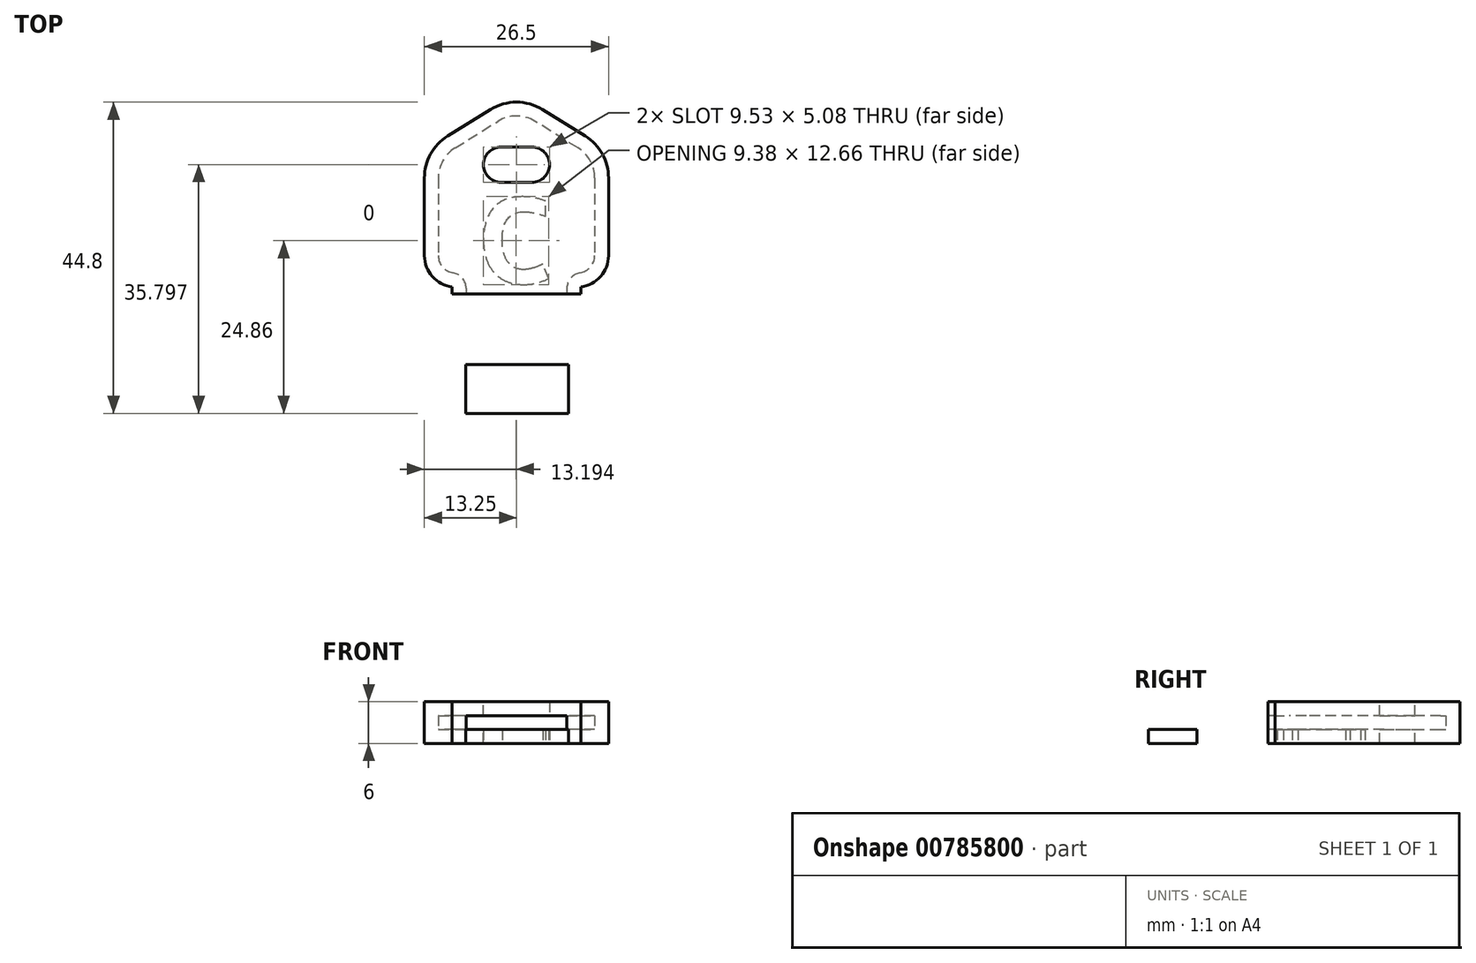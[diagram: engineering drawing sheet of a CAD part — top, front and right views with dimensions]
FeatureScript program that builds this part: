
annotation { "Feature Type Name" : "Feature", "Feature Type Description" : "" }
export const myFeature = defineFeature(function(context is Context, id is Id, definition is map)
    precondition{}
    {
        {
            var Q0;
            Q0=qCreatedBy(makeId("Top.planeOp"),FACE);
            var sketch = newSketch(context, id + "F0", { "sketchPlane" : qUnion([Q0])});
            skLineSegment(sketch, "E0.bottom", {"start": v(-11.25, 18.93) * mm, "end": v(11.25, 18.93) * mm});
            skLineSegment(sketch, "E0.top", {"start": v(-11.25, -7.57) * mm, "end": v(11.25, -7.57) * mm});
            skLineSegment(sketch, "E0.left", {"start": v(-11.25, 18.93) * mm, "end": v(-11.25, -7.57) * mm});
            skLineSegment(sketch, "E0.right", {"start": v(11.25, 18.93) * mm, "end": v(11.25, -7.57) * mm});
            skSolve(sketch);
        }
        {
            var Q0;
            Q0 = qSketchRegion(id + "F0", true);
            extrude(context, id + "F1", {"entities" : qUnion([Q0]), "depth" : 2 * mm, "offsetDistance" : 25.4 * mm});
        }
        {
            var Q0;
            Q0=makeQuery(id+"F1.opExtrude","SWEPT_EDGE",EDGE,{"disambiguationData":[OSD([sQuery(id+"F0.wireOp",EDGE,"E0.bottom"),sQuery(id+"F0.wireOp",EDGE,"E0.left")])]});
            var Q1;
            Q1=makeQuery(id+"F1.opExtrude","SWEPT_EDGE",EDGE,{"disambiguationData":[OSD([sQuery(id+"F0.wireOp",EDGE,"E0.bottom"),sQuery(id+"F0.wireOp",EDGE,"E0.right")])]});
            chamfer(context, id + "F2", {"entities" : qUnion([Q0, Q1]), "chamferType" : ChamferType.TWO_OFFSETS, "width1" : 22.5 * mm / 2, "oppositeDirection" : true, "width2" : 7 * mm, "tangentPropagation" : true});
        }
        {
            var Q0;
            {var subQ0=sQuery(id+"F0.wireOp",EDGE,"E0.bottom");Q0=makeQuery(id+"F2.opChamfer","BLEND_EDGE",EDGE,{"blendedFrom":[makeQuery(id+"F1.opExtrude","SWEPT_EDGE",EDGE,{"disambiguationData":[OSD([subQ0,sQuery(id+"F0.wireOp",EDGE,"E0.left")])]}),makeQuery(id+"F1.opExtrude","SWEPT_EDGE",EDGE,{"disambiguationData":[OSD([subQ0,sQuery(id+"F0.wireOp",EDGE,"E0.right")])]})],"blendedInto":[]});}
            var Q1;
            {var subQ0=sQuery(id+"F0.wireOp",EDGE,"E0.left");Q1=makeQuery(id+"F2.opChamfer","BLEND_EDGE",EDGE,{"blendedFrom":[makeQuery(id+"F1.opExtrude","SWEPT_EDGE",EDGE,{"disambiguationData":[OSD([sQuery(id+"F0.wireOp",EDGE,"E0.bottom"),subQ0])]}),makeQuery(id+"F1.opExtrude","SWEPT_FACE",FACE,{"disambiguationData":[OSD([subQ0])]})],"blendedInto":[makeQuery(id+"F1.opExtrude","SWEPT_FACE",FACE,{"disambiguationData":[OSD([subQ0])]})]});}
            var Q2;
            {var subQ0=sQuery(id+"F0.wireOp",EDGE,"E0.right");Q2=makeQuery(id+"F2.opChamfer","BLEND_EDGE",EDGE,{"blendedFrom":[makeQuery(id+"F1.opExtrude","SWEPT_EDGE",EDGE,{"disambiguationData":[OSD([sQuery(id+"F0.wireOp",EDGE,"E0.bottom"),subQ0])]}),makeQuery(id+"F1.opExtrude","SWEPT_FACE",FACE,{"disambiguationData":[OSD([subQ0])]})],"blendedInto":[makeQuery(id+"F1.opExtrude","SWEPT_FACE",FACE,{"disambiguationData":[OSD([subQ0])]})]});}
            fillet(context, id + "F3", {"entities" : qUnion([Q0, Q1, Q2]), "radius" : 5.08 * mm, "tangentPropagation" : true, "allowEdgeOverflow" : false});
        }
        {
            var Q0;
            Q0=makeQuery(id+"F1.opExtrude","CAP_FACE",FACE,{"disambiguationData":[OSD([sQuery(id+"F0.wireOp",EDGE,"E0.bottom"),sQuery(id+"F0.wireOp",EDGE,"E0.top"),sQuery(id+"F0.wireOp",EDGE,"E0.left"),sQuery(id+"F0.wireOp",EDGE,"E0.right")])],"isStart":false});
            var sketch = newSketch(context, id + "F4", { "sketchPlane" : qUnion([Q0])});
            skLineSegment(sketch, "E1.bottom", {"start": v(-15.5, -4.57) * mm, "end": v(-7.25, -4.57) * mm});
            skLineSegment(sketch, "E1.top", {"start": v(-15.5, -14.03) * mm, "end": v(-7.25, -14.03) * mm});
            skLineSegment(sketch, "E1.left", {"start": v(-15.5, -4.57) * mm, "end": v(-15.5, -14.03) * mm});
            skLineSegment(sketch, "E1.right", {"start": v(-7.25, -4.57) * mm, "end": v(-7.25, -14.03) * mm});
            skLineSegment(sketch, "E2.bottom", {"start": v(7.25, -4.57) * mm, "end": v(18.47, -4.57) * mm});
            skLineSegment(sketch, "E2.top", {"start": v(7.25, -15.42) * mm, "end": v(18.47, -15.42) * mm});
            skLineSegment(sketch, "E2.left", {"start": v(7.25, -4.57) * mm, "end": v(7.25, -15.42) * mm});
            skLineSegment(sketch, "E2.right", {"start": v(18.47, -4.57) * mm, "end": v(18.47, -15.42) * mm});
            skSolve(sketch);
        }
        {
            var Q0;
            Q0 = qSketchRegion(id + "F4", true);
            extrude(context, id + "F5", {"entities" : qUnion([Q0]), "operationType" : NewBodyOperationType.REMOVE, "oppositeDirection" : true, "depth" : 25.4 * mm, "offsetDistance" : 25.4 * mm});
        }
        {
            var Q0;
            Q0=makeQuery(id+"F5.boolean.opBoolean","INTERSECT",EDGE,{"derivedFrom":[makeQuery(id+"F1.opExtrude","SWEPT_FACE",FACE,{"disambiguationData":[OSD([sQuery(id+"F0.wireOp",EDGE,"E0.left")])]}),makeQuery(id+"F5.opExtrude","SWEPT_FACE",FACE,{"disambiguationData":[OSD([sQuery(id+"F4.wireOp",EDGE,"E1.bottom")])]})]});
            var Q1;
            Q1=makeQuery(id+"F5.boolean.opBoolean","INTERSECT",EDGE,{"derivedFrom":[makeQuery(id+"F1.opExtrude","SWEPT_FACE",FACE,{"disambiguationData":[OSD([sQuery(id+"F0.wireOp",EDGE,"E0.right")])]}),makeQuery(id+"F5.opExtrude","SWEPT_FACE",FACE,{"disambiguationData":[OSD([sQuery(id+"F4.wireOp",EDGE,"E2.bottom")])]})]});
            fillet(context, id + "F6", {"entities" : qUnion([Q0, Q1]), "radius" : 2.5 * mm, "tangentPropagation" : true, "allowEdgeOverflow" : false});
        }
        {
            var Q0;
            Q0=makeQuery(id+"F5.boolean.opBoolean","COPY",EDGE,{"derivedFrom":makeQuery(id+"F5.opExtrude","SWEPT_EDGE",EDGE,{"disambiguationData":[OSD([sQuery(id+"F4.wireOp",EDGE,"E1.bottom"),sQuery(id+"F4.wireOp",EDGE,"E1.right")])]})});
            var Q1;
            Q1=makeQuery(id+"F5.boolean.opBoolean","COPY",EDGE,{"derivedFrom":makeQuery(id+"F5.opExtrude","SWEPT_EDGE",EDGE,{"disambiguationData":[OSD([sQuery(id+"F4.wireOp",EDGE,"E2.bottom"),sQuery(id+"F4.wireOp",EDGE,"E2.left")])]})});
            fillet(context, id + "F7", {"entities" : qUnion([Q0, Q1]), "radius" : 2.25 * mm, "tangentPropagation" : true, "allowEdgeOverflow" : false});
        }
        {
            var Q0;
            Q0=makeQuery(id+"F1.opExtrude","CAP_FACE",FACE,{"disambiguationData":[OSD([sQuery(id+"F0.wireOp",EDGE,"E0.bottom"),sQuery(id+"F0.wireOp",EDGE,"E0.top"),sQuery(id+"F0.wireOp",EDGE,"E0.left"),sQuery(id+"F0.wireOp",EDGE,"E0.right")])],"isStart":false});
            var sketch = newSketch(context, id + "F8", { "sketchPlane" : qUnion([Q0])});
            skArc(sketch, "E3.0", {"start": v(-9.91, 15.12) * mm, "mid": v(-12.36, 12.55) * mm, "end": v(-13.25, 9.1) * mm});
            skLineSegment(sketch, "E3.1", {"start": v(9.25, -7.57) * mm, "end": v(9.25, -6.54) * mm});
            skLineSegment(sketch, "E3.2", {"start": v(-9.25, -7.57) * mm, "end": v(9.25, -7.57) * mm});
            skLineSegment(sketch, "E3.3", {"start": v(-9.25, -6.54) * mm, "end": v(-9.25, -7.57) * mm});
            skArc(sketch, "E3.4", {"start": v(-13.25, -2.07) * mm, "mid": v(-12.1, -5.07) * mm, "end": v(-9.25, -6.54) * mm});
            skArc(sketch, "E3.5", {"start": v(9.25, -6.54) * mm, "mid": v(12.1, -5.07) * mm, "end": v(13.25, -2.07) * mm});
            skLineSegment(sketch, "E3.6", {"start": v(-13.25, 9.1) * mm, "end": v(-13.25, -2.07) * mm});
            skLineSegment(sketch, "E3.7", {"start": v(13.25, -2.07) * mm, "end": v(13.25, 9.1) * mm});
            skArc(sketch, "E3.8", {"start": v(13.25, 9.1) * mm, "mid": v(12.36, 12.55) * mm, "end": v(9.91, 15.12) * mm});
            skLineSegment(sketch, "E3.9", {"start": v(9.91, 15.12) * mm, "end": v(3.74, 18.96) * mm});
            skArc(sketch, "E3.10", {"start": v(3.74, 18.96) * mm, "mid": v(0, 20.03) * mm, "end": v(-3.74, 18.96) * mm});
            skLineSegment(sketch, "E3.11", {"start": v(-3.74, 18.96) * mm, "end": v(-9.91, 15.12) * mm});
            skSolve(sketch);
        }
        {
            var Q0;
            Q0 = qSketchRegion(id + "F8", true);
            extrude(context, id + "F9", {"entities" : qUnion([Q0]), "depth" : 2 * mm, "offsetDistance" : 25.4 * mm, "hasSecondDirection" : true, "secondDirectionOppositeDirection" : true, "secondDirectionDepth" : 4 * mm});
        }
        {
            var Q0;
            Q0=makeQuery(id+"F1.opExtrude","SWEPT_BODY",BODY,{"disambiguationData":[OSD([sQuery(id+"F0.wireOp",EDGE,"E0.bottom"),sQuery(id+"F0.wireOp",EDGE,"E0.top"),sQuery(id+"F0.wireOp",EDGE,"E0.left"),sQuery(id+"F0.wireOp",EDGE,"E0.right")])]});
            var Q1;
            Q1=makeQuery(id+"F9.opExtrude","SWEPT_BODY",BODY,{"disambiguationData":[OSD([sQuery(id+"F8.wireOp",EDGE,"E3.0"),sQuery(id+"F8.wireOp",EDGE,"E3.1"),sQuery(id+"F8.wireOp",EDGE,"E3.2"),sQuery(id+"F8.wireOp",EDGE,"E3.3"),sQuery(id+"F8.wireOp",EDGE,"E3.4"),sQuery(id+"F8.wireOp",EDGE,"E3.5"),sQuery(id+"F8.wireOp",EDGE,"E3.6"),sQuery(id+"F8.wireOp",EDGE,"E3.7"),sQuery(id+"F8.wireOp",EDGE,"E3.8"),sQuery(id+"F8.wireOp",EDGE,"E3.9"),sQuery(id+"F8.wireOp",EDGE,"E3.10"),sQuery(id+"F8.wireOp",EDGE,"E3.11")])]});
            booleanBodies(context, id + "F10", {"operationType" : BooleanOperationType.SUBTRACTION, "tools" : qUnion([Q0]), "targets" : qUnion([Q1])});
        }
        {
            var Q0;
            Q0=makeQuery(id+"F9.opExtrude","CAP_FACE",FACE,{"disambiguationData":[OSD([sQuery(id+"F8.wireOp",EDGE,"E3.0"),sQuery(id+"F8.wireOp",EDGE,"E3.1"),sQuery(id+"F8.wireOp",EDGE,"E3.2"),sQuery(id+"F8.wireOp",EDGE,"E3.3"),sQuery(id+"F8.wireOp",EDGE,"E3.4"),sQuery(id+"F8.wireOp",EDGE,"E3.5"),sQuery(id+"F8.wireOp",EDGE,"E3.6"),sQuery(id+"F8.wireOp",EDGE,"E3.7"),sQuery(id+"F8.wireOp",EDGE,"E3.8"),sQuery(id+"F8.wireOp",EDGE,"E3.9"),sQuery(id+"F8.wireOp",EDGE,"E3.10"),sQuery(id+"F8.wireOp",EDGE,"E3.11")])],"isStart":true});
            var sketch = newSketch(context, id + "F11", { "sketchPlane" : qUnion([Q0])});
            skText(sketch, "E4", { "text": "C", "fontName": "OpenSans-Bold.ttf"});
            const initialGuessF11  = {"E4": [-0.00575, -0.00625, 1, 0, 0.01242]};
            skSetInitialGuess(sketch, initialGuessF11);
            skSolve(sketch);
        }
        {
            var Q0;
            Q0 = qSketchRegion(id + "F11", true);
            extrude(context, id + "F12", {"entities" : qUnion([Q0]), "operationType" : NewBodyOperationType.REMOVE, "endBound" : BoundingType.UP_TO_NEXT, "oppositeDirection" : true, "depth" : 25.4 * mm, "offsetDistance" : 25.4 * mm});
        }
        {
            var Q0;
            Q0=makeQuery(id+"F9.opExtrude","CAP_FACE",FACE,{"disambiguationData":[OSD([sQuery(id+"F8.wireOp",EDGE,"E3.0"),sQuery(id+"F8.wireOp",EDGE,"E3.1"),sQuery(id+"F8.wireOp",EDGE,"E3.2"),sQuery(id+"F8.wireOp",EDGE,"E3.3"),sQuery(id+"F8.wireOp",EDGE,"E3.4"),sQuery(id+"F8.wireOp",EDGE,"E3.5"),sQuery(id+"F8.wireOp",EDGE,"E3.6"),sQuery(id+"F8.wireOp",EDGE,"E3.7"),sQuery(id+"F8.wireOp",EDGE,"E3.8"),sQuery(id+"F8.wireOp",EDGE,"E3.9"),sQuery(id+"F8.wireOp",EDGE,"E3.10"),sQuery(id+"F8.wireOp",EDGE,"E3.11")])],"isStart":false});
            var sketch = newSketch(context, id + "F13", { "sketchPlane" : qUnion([Q0])});
            skPoint(sketch, "E5", {"position": v(0, 11.03) * mm});
            skLineSegment(sketch, "E6.bottom", {"start": v(4.76, 13.57) * mm, "end": v(-4.76, 13.57) * mm});
            skLineSegment(sketch, "E6.top", {"start": v(4.76, 8.49) * mm, "end": v(-4.76, 8.49) * mm});
            skLineSegment(sketch, "E6.left", {"start": v(4.76, 13.57) * mm, "end": v(4.76, 8.49) * mm});
            skLineSegment(sketch, "E6.right", {"start": v(-4.76, 13.57) * mm, "end": v(-4.76, 8.49) * mm});
            skSolve(sketch);
        }
        {
            var Q0;
            Q0=sQuery(id+"F13.wireOp",VERTEX,"E5");
            var Q1;
            Q1=makeQuery(id+"F9.opExtrude","SWEPT_BODY",BODY,{"disambiguationData":[OSD([sQuery(id+"F8.wireOp",EDGE,"E3.0"),sQuery(id+"F8.wireOp",EDGE,"E3.1"),sQuery(id+"F8.wireOp",EDGE,"E3.2"),sQuery(id+"F8.wireOp",EDGE,"E3.3"),sQuery(id+"F8.wireOp",EDGE,"E3.4"),sQuery(id+"F8.wireOp",EDGE,"E3.5"),sQuery(id+"F8.wireOp",EDGE,"E3.6"),sQuery(id+"F8.wireOp",EDGE,"E3.7"),sQuery(id+"F8.wireOp",EDGE,"E3.8"),sQuery(id+"F8.wireOp",EDGE,"E3.9"),sQuery(id+"F8.wireOp",EDGE,"E3.10"),sQuery(id+"F8.wireOp",EDGE,"E3.11")])]});
            hole(context, id + "F14", {"style" : HoleStyle.SIMPLE, "endStyle" : HoleEndStyle.THROUGH, "holeDiameter" : 5.08 * mm, "majorDiameter" : 6.35 * mm, "isTappedThrough" : true, "tappedDepth" : 12.7 * mm, "tapClearance" : 3, "locations" : qUnion([Q0]), "scope" : qUnion([Q1])});
        }
        {
            var Q0;
            Q0 = qSketchRegion(id + "F13", true);
            extrude(context, id + "F15", {"entities" : qUnion([Q0]), "operationType" : NewBodyOperationType.REMOVE, "endBound" : BoundingType.THROUGH_ALL, "oppositeDirection" : true, "depth" : 25.4 * mm, "offsetDistance" : 25.4 * mm});
        }
        {
            var Q0;
            {var subQ0=sQuery(id+"F13.wireOp",EDGE,"E6.right");var subQ1=sQuery(id+"F13.wireOp",EDGE,"E6.top");Q0=makeQuery(id+"F15.boolean.opBoolean","COPY",EDGE,{"disambiguationData":[TD([makeQuery(id+"F10.opBoolean","COPY",FACE,{"derivedFrom":makeQuery(id+"F1.opExtrude","CAP_FACE",FACE,{"disambiguationData":[OSD([sQuery(id+"F0.wireOp",EDGE,"E0.bottom"),sQuery(id+"F0.wireOp",EDGE,"E0.top"),sQuery(id+"F0.wireOp",EDGE,"E0.left"),sQuery(id+"F0.wireOp",EDGE,"E0.right")])],"isStart":true})})])],"derivedFrom":makeQuery(id+"F15.opExtrude","SWEPT_EDGE",EDGE,{"disambiguationData":[OSD([subQ1,subQ0])]})});}
            var Q1;
            {var subQ0=sQuery(id+"F13.wireOp",EDGE,"E6.top");var subQ1=sQuery(id+"F13.wireOp",EDGE,"E6.right");Q1=makeQuery(id+"F15.boolean.opBoolean","COPY",EDGE,{"disambiguationData":[TD([makeQuery(id+"F10.opBoolean","COPY",FACE,{"derivedFrom":makeQuery(id+"F1.opExtrude","CAP_FACE",FACE,{"disambiguationData":[OSD([sQuery(id+"F0.wireOp",EDGE,"E0.bottom"),sQuery(id+"F0.wireOp",EDGE,"E0.top"),sQuery(id+"F0.wireOp",EDGE,"E0.left"),sQuery(id+"F0.wireOp",EDGE,"E0.right")])],"isStart":false})})])],"derivedFrom":makeQuery(id+"F15.opExtrude","SWEPT_EDGE",EDGE,{"disambiguationData":[OSD([subQ0,subQ1])]})});}
            var Q2;
            {var subQ0=sQuery(id+"F13.wireOp",EDGE,"E6.top");var subQ1=sQuery(id+"F13.wireOp",EDGE,"E6.left");Q2=makeQuery(id+"F15.boolean.opBoolean","COPY",EDGE,{"disambiguationData":[TD([makeQuery(id+"F10.opBoolean","COPY",FACE,{"derivedFrom":makeQuery(id+"F1.opExtrude","CAP_FACE",FACE,{"disambiguationData":[OSD([sQuery(id+"F0.wireOp",EDGE,"E0.bottom"),sQuery(id+"F0.wireOp",EDGE,"E0.top"),sQuery(id+"F0.wireOp",EDGE,"E0.left"),sQuery(id+"F0.wireOp",EDGE,"E0.right")])],"isStart":true})})])],"derivedFrom":makeQuery(id+"F15.opExtrude","SWEPT_EDGE",EDGE,{"disambiguationData":[OSD([subQ0,subQ1])]})});}
            var Q3;
            {var subQ0=sQuery(id+"F13.wireOp",EDGE,"E6.top");var subQ1=sQuery(id+"F13.wireOp",EDGE,"E6.left");Q3=makeQuery(id+"F15.boolean.opBoolean","COPY",EDGE,{"disambiguationData":[TD([makeQuery(id+"F10.opBoolean","COPY",FACE,{"derivedFrom":makeQuery(id+"F1.opExtrude","CAP_FACE",FACE,{"disambiguationData":[OSD([sQuery(id+"F0.wireOp",EDGE,"E0.bottom"),sQuery(id+"F0.wireOp",EDGE,"E0.top"),sQuery(id+"F0.wireOp",EDGE,"E0.left"),sQuery(id+"F0.wireOp",EDGE,"E0.right")])],"isStart":false})})])],"derivedFrom":makeQuery(id+"F15.opExtrude","SWEPT_EDGE",EDGE,{"disambiguationData":[OSD([subQ0,subQ1])]})});}
            var Q4;
            {var subQ0=sQuery(id+"F13.wireOp",EDGE,"E6.bottom");var subQ1=sQuery(id+"F13.wireOp",EDGE,"E6.left");Q4=makeQuery(id+"F15.boolean.opBoolean","COPY",EDGE,{"disambiguationData":[TD([makeQuery(id+"F10.opBoolean","COPY",FACE,{"derivedFrom":makeQuery(id+"F1.opExtrude","CAP_FACE",FACE,{"disambiguationData":[OSD([sQuery(id+"F0.wireOp",EDGE,"E0.bottom"),sQuery(id+"F0.wireOp",EDGE,"E0.top"),sQuery(id+"F0.wireOp",EDGE,"E0.left"),sQuery(id+"F0.wireOp",EDGE,"E0.right")])],"isStart":true})})])],"derivedFrom":makeQuery(id+"F15.opExtrude","SWEPT_EDGE",EDGE,{"disambiguationData":[OSD([subQ0,subQ1])]})});}
            var Q5;
            {var subQ0=sQuery(id+"F13.wireOp",EDGE,"E6.bottom");var subQ1=sQuery(id+"F13.wireOp",EDGE,"E6.left");Q5=makeQuery(id+"F15.boolean.opBoolean","COPY",EDGE,{"disambiguationData":[TD([makeQuery(id+"F10.opBoolean","COPY",FACE,{"derivedFrom":makeQuery(id+"F1.opExtrude","CAP_FACE",FACE,{"disambiguationData":[OSD([sQuery(id+"F0.wireOp",EDGE,"E0.bottom"),sQuery(id+"F0.wireOp",EDGE,"E0.top"),sQuery(id+"F0.wireOp",EDGE,"E0.left"),sQuery(id+"F0.wireOp",EDGE,"E0.right")])],"isStart":false})})])],"derivedFrom":makeQuery(id+"F15.opExtrude","SWEPT_EDGE",EDGE,{"disambiguationData":[OSD([subQ0,subQ1])]})});}
            var Q6;
            {var subQ0=sQuery(id+"F13.wireOp",EDGE,"E6.bottom");var subQ1=sQuery(id+"F13.wireOp",EDGE,"E6.right");Q6=makeQuery(id+"F15.boolean.opBoolean","COPY",EDGE,{"disambiguationData":[TD([makeQuery(id+"F10.opBoolean","COPY",FACE,{"derivedFrom":makeQuery(id+"F1.opExtrude","CAP_FACE",FACE,{"disambiguationData":[OSD([sQuery(id+"F0.wireOp",EDGE,"E0.bottom"),sQuery(id+"F0.wireOp",EDGE,"E0.top"),sQuery(id+"F0.wireOp",EDGE,"E0.left"),sQuery(id+"F0.wireOp",EDGE,"E0.right")])],"isStart":true})})])],"derivedFrom":makeQuery(id+"F15.opExtrude","SWEPT_EDGE",EDGE,{"disambiguationData":[OSD([subQ0,subQ1])]})});}
            var Q7;
            {var subQ0=sQuery(id+"F13.wireOp",EDGE,"E6.bottom");var subQ1=sQuery(id+"F13.wireOp",EDGE,"E6.right");Q7=makeQuery(id+"F15.boolean.opBoolean","COPY",EDGE,{"disambiguationData":[TD([makeQuery(id+"F10.opBoolean","COPY",FACE,{"derivedFrom":makeQuery(id+"F1.opExtrude","CAP_FACE",FACE,{"disambiguationData":[OSD([sQuery(id+"F0.wireOp",EDGE,"E0.bottom"),sQuery(id+"F0.wireOp",EDGE,"E0.top"),sQuery(id+"F0.wireOp",EDGE,"E0.left"),sQuery(id+"F0.wireOp",EDGE,"E0.right")])],"isStart":false})})])],"derivedFrom":makeQuery(id+"F15.opExtrude","SWEPT_EDGE",EDGE,{"disambiguationData":[OSD([subQ0,subQ1])]})});}
            fillet(context, id + "F16", {"entities" : qUnion([Q0, Q1, Q2, Q3, Q4, Q5, Q6, Q7]), "radius" : 2.54 * mm, "tangentPropagation" : true, "allowEdgeOverflow" : false});
        }
        {
            var Q0;
            Q0=makeQuery(id+"F9.opExtrude","CAP_FACE",FACE,{"disambiguationData":[OSD([sQuery(id+"F8.wireOp",EDGE,"E3.0"),sQuery(id+"F8.wireOp",EDGE,"E3.1"),sQuery(id+"F8.wireOp",EDGE,"E3.2"),sQuery(id+"F8.wireOp",EDGE,"E3.3"),sQuery(id+"F8.wireOp",EDGE,"E3.4"),sQuery(id+"F8.wireOp",EDGE,"E3.5"),sQuery(id+"F8.wireOp",EDGE,"E3.6"),sQuery(id+"F8.wireOp",EDGE,"E3.7"),sQuery(id+"F8.wireOp",EDGE,"E3.8"),sQuery(id+"F8.wireOp",EDGE,"E3.9"),sQuery(id+"F8.wireOp",EDGE,"E3.10"),sQuery(id+"F8.wireOp",EDGE,"E3.11")])],"isStart":true});
            var sketch = newSketch(context, id + "F17", { "sketchPlane" : qUnion([Q0])});
            skLineSegment(sketch, "E7.bottom", {"start": v(-7.3, 17.77) * mm, "end": v(7.5, 17.77) * mm});
            skLineSegment(sketch, "E7.top", {"start": v(-7.3, 24.77) * mm, "end": v(7.5, 24.77) * mm});
            skLineSegment(sketch, "E7.left", {"start": v(-7.3, 17.77) * mm, "end": v(-7.3, 24.77) * mm});
            skLineSegment(sketch, "E7.right", {"start": v(7.5, 17.77) * mm, "end": v(7.5, 24.77) * mm});
            skSolve(sketch);
        }
        {
            var Q0;
            Q0 = qSketchRegion(id + "F17", true);
            extrude(context, id + "F18", {"entities" : qUnion([Q0]), "oppositeDirection" : true, "depth" : 2 * mm, "offsetDistance" : 25.4 * mm});
        }
    });
